# Revit family: Domotics-DomesticRanges-GEWISS-CHORUS_COMMAND-DIMMER_ROTATING
name_source: partatom
category: Apparecchi elettrici
revit_build: Autodesk Revit 2016 (Build: 20161004_0715(x64)
units: mm (PartAtom-declared; Revit-internal decimal feet)

## family parameters
Condiviso = Sì
Host = Superficie
Mantenere orientamento annotazione = Sì
Punto di calcolo locali = Sì
Quota connettore circolare = Usa diametro
Taglio con vuoti quando caricato = Sì
Tipo di parte = Normale

## types (12) — shared parameters
Carico apparente = 0 VA
Catalogue = DOMOTICS
Catalogue Range = CHORUS - DOMESTIC RANGE
IDF = e04840bd-86cc-4d9d-9857-066b079db0ba
IDT = 557559c5-ec2b-4e0f-8006-e2e8f87050b4
Immagine tipo = GW14561.jpg
N. poli = 1
No. Chorus modules: = 1
Produttore = GEWISS S.p.A.
Prospetto di default = 1219 mm
Technical sheet = https://www.gewiss.com
Tipo = CHORUS DIMMER ROTATIVO_GENERALE : GW14567 Regolatore elettronico rotativo deviatore 1M 100-500W titanio
Tipo simbolo = PULSANTI : DIMMMANOP
URL = https://www.gewiss.com
Version file RFA = 19.0
Volt = 230 V

## per-type parameters (varying)
| type | Colour | Command | Control | Description. | Descrizione | EAN code | Electrocod | Inductive load | Inductive load 230V ac | Load type | Modello | No. Chorus modules | Resistive load | Resistive load 230V ac | SEO | Supply voltage |
| GW12561 - Electronic regulator rotating 1M 100-500W Black | Black | Rotary | Rotary | Rotary dimmer | ROTATING ELEC REGULATOR 1M 100-500W B | 8011564268265 | 0141 |  |  | Resistive | GW12561 | 1 | 100 - 500 W | 100 - 500 W | Dimmer | 230 V ac - 50/60 Hz |
| GW12567 - Electronic regulator rotating with 2-way switch 1M 100-500W Black | Black | Rotary | Rotary | Rotary dimmer | ROT ELEC REG 2-WAY SWITCH 1M 100-500W B | 8011564268296 | 0130 | 100 - 500 VA | 100 - 500 VA | Resistive/Inductive | GW12567 | 1 | 100 - 500 W | 100 - 500 W | Dimmer | 230 V ac - 50/60 Hz |
| GW12566 - ELEC. UNIVERSAL REGULATOR 1M BLACK |  |  |  |  | ELEC. UNIVERSAL REGULATOR 1M BLACK | 8011564895140 | 0141 |  |  |  | GW12566 |  |  |  | Dimmer | 230V ac - 50Hz |
| GW12564 - Electronic regulator rotating 1M 100-900W Black | Black | Rotary | Rotary | Rotary dimmer | ROTATING ELEC REGULATOR 1M 100-900W B | 8011564268272 | 0141 | 40 - 300 VA | 40 - 300 VA | Resistive/Inductive | GW12564 | 1 | 100 - 900 W | 100 - 900 W | Dimmer | 230 V ac - 50/60 Hz |
| GW14567 - Electronic regulator rotating with 2-way switch 1M 100-500W Titanium | Titanium | Rotary | Rotary | Rotary dimmer | ROT ELEC REG 2-WAY SWITCH, 1M 100-500W T | 8011564267985 | 0130 | 100 - 500 VA | 100 - 500 VA | Resistive/Inductive | GW14567 | 1 | 100 - 500 W | 100 - 500 W | Dimmer | 230 V ac - 50/60 Hz |
| GW10566 - ELEC. UNIVERSAL REGULATOR 1M WHITE |  |  |  |  | ELEC. UNIVERSAL REGULATOR 1M WHITE | 8011564895126 | 0781 |  |  |  | GW10566 |  |  |  | Dimmer | 230V ac - 50Hz |
| GW10564 - Electronic regulator rotating 1M 100-900W White | White | Rotary | Rotary | Rotary dimmer | ROTATING ELEC REGULATOR 1M 100-900W W | 8011564263062 | 0781 | 40 - 300 VA | 40 - 300 VA | Resistive/Inductive | GW10564 | 1 | 100 - 900 W | 100 - 900 W | Dimmer | 230 V ac - 50/60 Hz |
| GW14564 - Electronic regulator rotating 1M 100-900W Titanium | Titanium | Rotary | Rotary | Rotary dimmer | ROTATING ELEC REGULATOR, 1M 100-900W T | 8011564267978 | 0141 | 40 - 300 VA | 40 - 300 VA | Resistive/Inductive | GW14564 | 1 | 100 - 900 W | 100 - 900 W | Dimmer | 230 V ac - 50/60 Hz |
| GW10567 - Electronic regulator rotating with 2-way switch 1M 100-500W White | White | Rotary | Rotary | Rotary dimmer | ROT ELEC REG 2-WAY SWITCH 1M 100-500W W | 8011564261099 | 0781 | 100 - 500 VA | 100 - 500 VA | Resistive/Inductive | GW10567 | 1 | 100 - 500 W | 100 - 500 W | Dimmer | 230 V ac - 50/60 Hz |
| GW14566 - ELEC. UNIVERSAL REGULATOR 1M TITANIUM |  |  |  |  | ELEC. UNIVERSAL REGULATOR 1M TITANIUM | 8011564895157 | 0141 |  |  |  | GW14566 |  |  |  | Relay | 230V ac - 50Hz |
| GW14561 - Electronic regulator rotating 1M 100-500W Titanium | Titanium | Rotary | Rotary | Rotary dimmer | ROTATING ELEC REGULATOR, 1M 100-500W T | 8011564267961 | 0141 |  |  | Resistive | GW14561 | 1 | 100 - 500 W | 100 - 500 W | Dimmer | 230 V ac - 50/60 Hz |
| GW10561 - Electronic regulator rotating 1M 100-500W White | White | Rotary | Rotary | Rotary dimmer | ROTATING ELEC REGULATOR 1M 100-500W W | 8011564263055 | 0781 |  |  | Resistive | GW10561 | 1 | 100 - 500 W | 100 - 500 W | Dimmer | 230 V ac - 50/60 Hz |

## geometry (parser evidence)
native form markers: Sweep x1
no freeform markers — native parametric forms only
